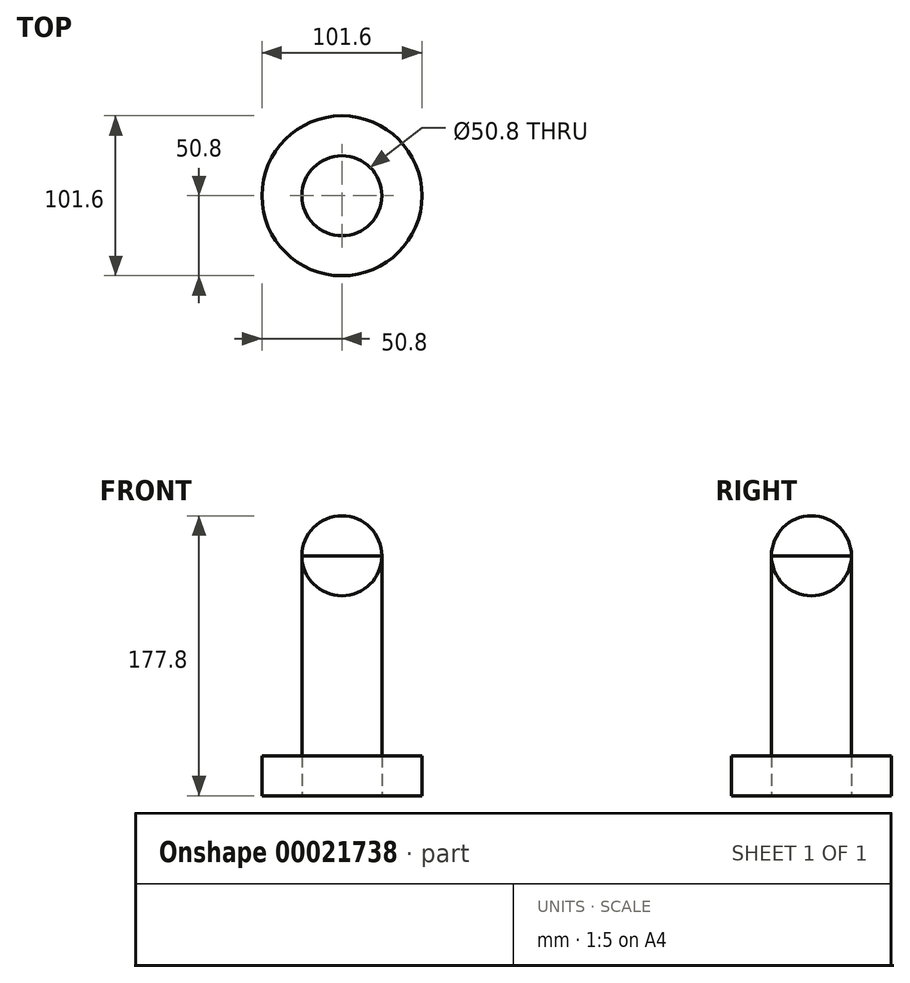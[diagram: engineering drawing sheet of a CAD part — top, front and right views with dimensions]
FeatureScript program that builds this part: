
annotation { "Feature Type Name" : "Feature", "Feature Type Description" : "" }
export const myFeature = defineFeature(function(context is Context, id is Id, definition is map)
    precondition{}
    {
        {
            var Q0;
            Q0=qCreatedBy(makeId("Top.planeOp"),FACE);
            var sketch = newSketch(context, id + "F0", { "sketchPlane" : qUnion([Q0])});
            skCircle(sketch, "E0", {"center": v(0, 0) * mm, "radius": 50.8 * mm});
            skCircle(sketch, "E1", {"center": v(0, 0) * mm, "radius": 25.4 * mm});
            skSolve(sketch);
        }
        {
            var Q0;
            Q0=makeQuery(id+"F0.imprint","IMPRINT",FACE,{"disambiguationData":[TD([[makeQuery(id+"F0.imprint","IMPRINT",EDGE,{"derivedFrom":sQuery(id+"F0.wireOp",EDGE,"E1")}),1.0]])]});
            extrude(context, id + "F1", {"entities" : qUnion([Q0]), "depth" : 152.4 * mm});
        }
        {
            var Q0;
            Q0 = qSketchRegion(id + "F0", true);
            extrude(context, id + "F2", {"entities" : qUnion([Q0]), "depth" : 25.4 * mm});
        }
        {
            var Q0;
            Q0=qCreatedBy(makeId("Top.planeOp"),FACE);
            cPlane(context, id + "F3", {"entities" : qUnion([Q0]), "cplaneType" : CPlaneType.OFFSET, "offset" : 152.4 * mm, "width" : 152.4 * mm, "height" : 152.4 * mm});
        }
        {
            var Q0;
            Q0=qCreatedBy(id+"F3.planeOp",FACE);
            var sketch = newSketch(context, id + "F4", { "sketchPlane" : qUnion([Q0])});
            skArc(sketch, "E2", {"start": v(25.4, 0) * mm, "mid": v(0, 25.4) * mm, "end": v(-25.4, 0) * mm});
            skLineSegment(sketch, "E3", {"start": v(-50.81, 0) * mm, "end": v(67.99, 0) * mm});
            skSolve(sketch);
        }
        {
            var Q0;
            Q0 = qSketchRegion(id + "F4", true);
            var Q1;
            Q1=sQuery(id+"F4.wireOp",EDGE,"E3");
            revolve(context, id + "F5", {"entities" : qUnion([Q0]), "axis" : qUnion([Q1]), "revolveType" : RevolveType.FULL});
        }
    });
